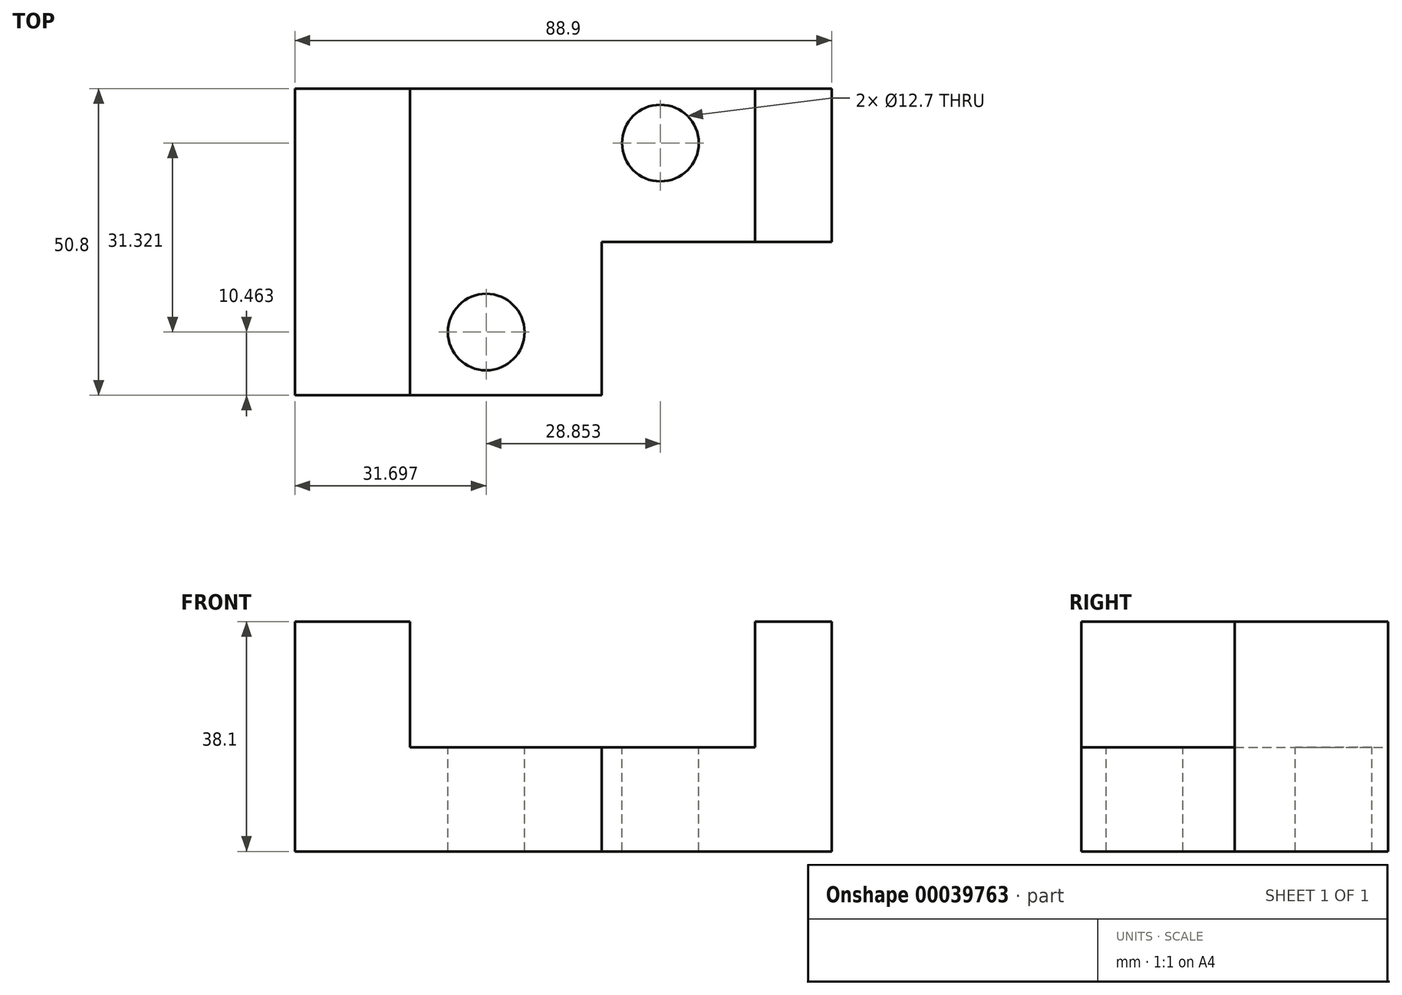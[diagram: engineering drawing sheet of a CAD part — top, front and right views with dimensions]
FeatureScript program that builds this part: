
annotation { "Feature Type Name" : "Feature", "Feature Type Description" : "" }
export const myFeature = defineFeature(function(context is Context, id is Id, definition is map)
    precondition{}
    {
        {
            var Q0;
            Q0=qCreatedBy(makeId("Front.planeOp"),FACE);
            var sketch = newSketch(context, id + "F0", { "sketchPlane" : qUnion([Q0])});
            skLineSegment(sketch, "E0", {"start": v(-60.55, 3.66) * mm, "end": v(-60.55, -34.44) * mm});
            skLineSegment(sketch, "E1", {"start": v(-60.55, -34.44) * mm, "end": v(28.35, -34.44) * mm});
            skLineSegment(sketch, "E2", {"start": v(28.35, -34.44) * mm, "end": v(28.35, 3.66) * mm});
            skLineSegment(sketch, "E3", {"start": v(28.35, 3.66) * mm, "end": v(15.65, 3.66) * mm});
            skLineSegment(sketch, "E4", {"start": v(15.65, 3.66) * mm, "end": v(15.65, -17.22) * mm});
            skLineSegment(sketch, "E5", {"start": v(15.65, -17.22) * mm, "end": v(-41.5, -17.22) * mm});
            skLineSegment(sketch, "E6", {"start": v(-41.5, -17.22) * mm, "end": v(-41.5, 3.66) * mm});
            skLineSegment(sketch, "E7", {"start": v(-41.5, 3.66) * mm, "end": v(-60.55, 3.66) * mm});
            skSolve(sketch);
        }
        {
            var Q0;
            Q0 = qSketchRegion(id + "F0", true);
            extrude(context, id + "F1", {"entities" : qUnion([Q0]), "depth" : 50.8 * mm});
        }
        {
            var Q0;
            Q0=makeQuery(id+"F1.opExtrude","SWEPT_FACE",FACE,{"disambiguationData":[OSD([sQuery(id+"F0.wireOp",EDGE,"E1")])]});
            var sketch = newSketch(context, id + "F2", { "sketchPlane" : qUnion([Q0])});
            skLineSegment(sketch, "E8.bottom", {"start": v(-9.75, 50.8) * mm, "end": v(28.35, 50.8) * mm});
            skLineSegment(sketch, "E8.top", {"start": v(-9.75, 25.4) * mm, "end": v(28.35, 25.4) * mm});
            skLineSegment(sketch, "E8.left", {"start": v(-9.75, 50.8) * mm, "end": v(-9.75, 25.4) * mm});
            skLineSegment(sketch, "E8.right", {"start": v(28.35, 50.8) * mm, "end": v(28.35, 25.4) * mm});
            skPoint(sketch, "E9", {"position": v(-28.8, 38.1) * mm});
            skPoint(sketch, "E10", {"position": v(-22.45, 12.7) * mm});
            skSolve(sketch);
        }
        {
            var Q0;
            Q0 = qSketchRegion(id + "F2", true);
            extrude(context, id + "F3", {"entities" : qUnion([Q0]), "operationType" : NewBodyOperationType.REMOVE, "endBound" : BoundingType.THROUGH_ALL, "oppositeDirection" : true, "depth" : 25.4 * mm});
        }
        {
            var Q0;
            Q0=makeQuery(id+"F1.opExtrude","SWEPT_FACE",FACE,{"disambiguationData":[OSD([sQuery(id+"F0.wireOp",EDGE,"E5")])]});
            var sketch = newSketch(context, id + "F4", { "sketchPlane" : qUnion([Q0])});
            skPoint(sketch, "E11", {"position": v(-28.85, -40.34) * mm});
            skPoint(sketch, "E12", {"position": v(0, -9.02) * mm});
            skSolve(sketch);
        }
        {
            var Q0;
            Q0=sQuery(id+"F4.wireOp",VERTEX,"E11");
            var Q1;
            Q1=sQuery(id+"F4.wireOp",VERTEX,"E12");
            var Q2;
            Q2=makeQuery(id+"F1.opExtrude","SWEPT_BODY",BODY,{"disambiguationData":[OSD([sQuery(id+"F0.wireOp",EDGE,"E0"),sQuery(id+"F0.wireOp",EDGE,"E1"),sQuery(id+"F0.wireOp",EDGE,"E2"),sQuery(id+"F0.wireOp",EDGE,"E3"),sQuery(id+"F0.wireOp",EDGE,"E4"),sQuery(id+"F0.wireOp",EDGE,"E5"),sQuery(id+"F0.wireOp",EDGE,"E6"),sQuery(id+"F0.wireOp",EDGE,"E7")])]});
            hole(context, id + "F5", {"style" : HoleStyle.SIMPLE, "holeDiameter" : 12.7 * mm, "endStyle" : HoleEndStyle.THROUGH, "locations" : qUnion([Q0, Q1]), "scope" : qUnion([Q2])});
        }
    });
